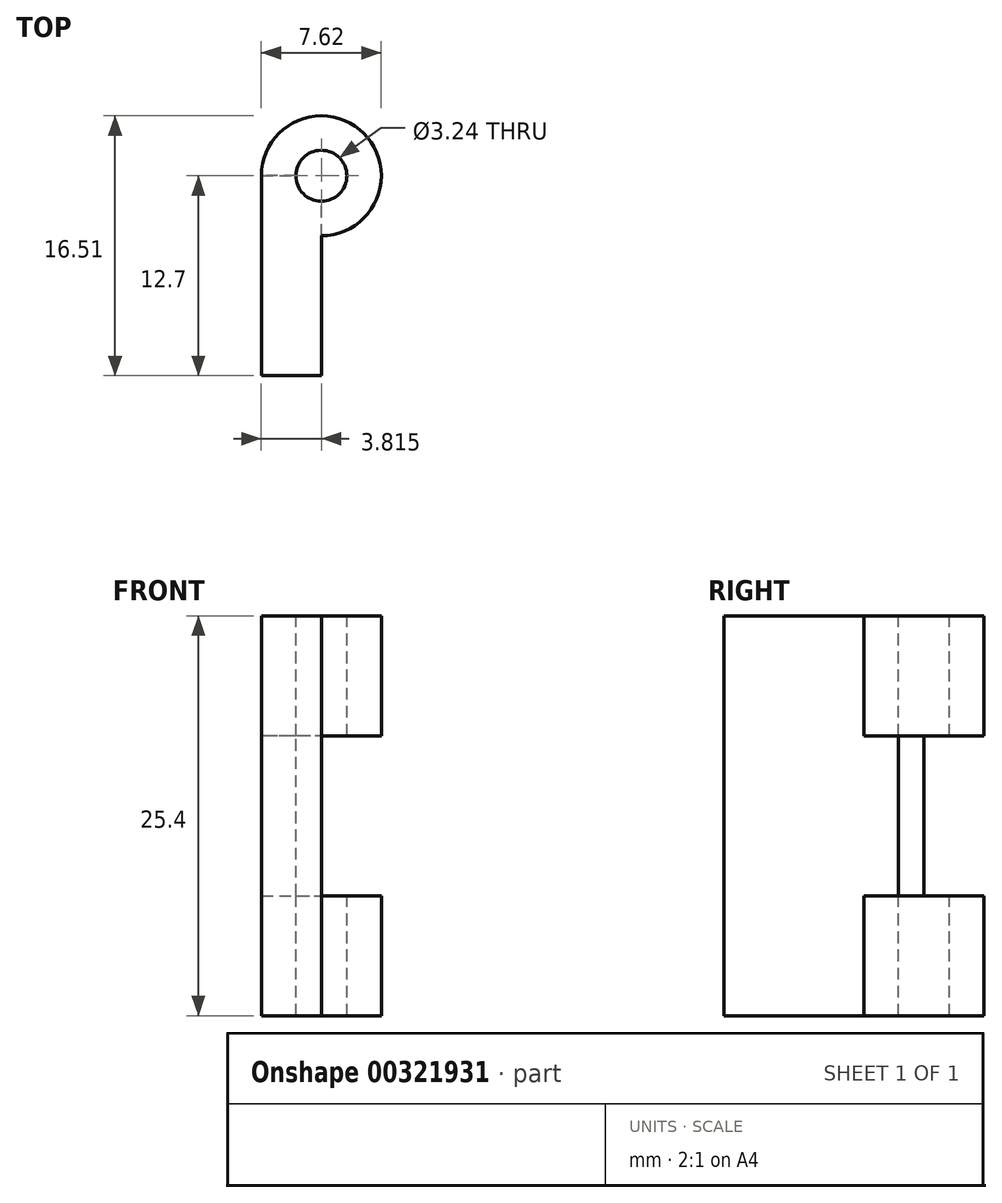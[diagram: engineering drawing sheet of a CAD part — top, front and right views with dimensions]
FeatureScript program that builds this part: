
annotation { "Feature Type Name" : "Feature", "Feature Type Description" : "" }
export const myFeature = defineFeature(function(context is Context, id is Id, definition is map)
    precondition{}
    {
        {
            var Q0;
            Q0=qCreatedBy(makeId("Front.planeOp"),FACE);
            var sketch = newSketch(context, id + "F0", { "sketchPlane" : qUnion([Q0])});
            skLineSegment(sketch, "E0.bottom", {"start": v(-1.9, -12.7) * mm, "end": v(1.9, -12.7) * mm});
            skLineSegment(sketch, "E0.top", {"start": v(-1.9, 12.7) * mm, "end": v(1.9, 12.7) * mm});
            skLineSegment(sketch, "E0.left", {"start": v(-1.9, -12.7) * mm, "end": v(-1.9, 12.7) * mm});
            skLineSegment(sketch, "E0.right", {"start": v(1.9, -12.7) * mm, "end": v(1.9, 12.7) * mm});
            skPoint(sketch, "E0.middle", {"position": v(0, 0) * mm});
            skSolve(sketch);
        }
        {
            var Q0;
            Q0 = qSketchRegion(id + "F0", true);
            extrude(context, id + "F1", {"entities" : qUnion([Q0]), "depth" : 12.7 * mm});
        }
        {
            var Q0;
            Q0=makeQuery(id+"F1.opExtrude","SWEPT_FACE",FACE,{"disambiguationData":[OSD([sQuery(id+"F0.wireOp",EDGE,"E0.top")])]});
            var sketch = newSketch(context, id + "F2", { "sketchPlane" : qUnion([Q0])});
            skCircle(sketch, "E1", {"center": v(1.9, 0) * mm, "radius": 3.81 * mm});
            skSolve(sketch);
        }
        {
            var Q0;
            Q0 = qSketchRegion(id + "F2", true);
            extrude(context, id + "F3", {"entities" : qUnion([Q0]), "operationType" : NewBodyOperationType.ADD, "oppositeDirection" : true, "depth" : 7.62 * mm});
        }
        {
            var Q0;
            Q0=makeQuery(id+"F1.opExtrude","SWEPT_FACE",FACE,{"disambiguationData":[OSD([sQuery(id+"F0.wireOp",EDGE,"E0.bottom")])]});
            var sketch = newSketch(context, id + "F4", { "sketchPlane" : qUnion([Q0])});
            skCircle(sketch, "E2", {"center": v(1.9, 0) * mm, "radius": 3.81 * mm});
            skSolve(sketch);
        }
        {
            var Q0;
            Q0 = qSketchRegion(id + "F2", true);
            extrude(context, id + "F5", {"entities" : qUnion([Q0]), "operationType" : NewBodyOperationType.ADD, "oppositeDirection" : true, "depth" : 7.62 * mm});
        }
        {
            var Q0;
            {var subQ1=sQuery(id+"F0.wireOp",EDGE,"E0.bottom");var subQ2=makeQuery(id+"F1.opExtrude","CAP_EDGE",EDGE,{"disambiguationData":[OSD([subQ1])],"isStart":true});Q0=makeQuery(id+"F4.imprint","IMPRINT",FACE,{"disambiguationData":[TD([[makeQuery(id+"F4.imprint","IMPRINT",EDGE,{"derivedFrom":subQ2}),-1.0]])]});}
            extrude(context, id + "F6", {"entities" : qUnion([Q0]), "operationType" : NewBodyOperationType.ADD, "oppositeDirection" : true, "depth" : 7.62 * mm});
        }
        {
            var Q0;
            Q0=makeQuery(id+"F3.boolean.opBoolean","MERGE",FACE,{"derivedFrom":[makeQuery(id+"F1.opExtrude","SWEPT_FACE",FACE,{"disambiguationData":[OSD([sQuery(id+"F0.wireOp",EDGE,"E0.top")])]}),makeQuery(id+"F3.opExtrude","CAP_FACE",FACE,{"disambiguationData":[OSD([sQuery(id+"F2.wireOp",EDGE,"E1")])],"isStart":true})]});
            var sketch = newSketch(context, id + "F7", { "sketchPlane" : qUnion([Q0])});
            skLineSegment(sketch, "E3", {"start": v(1.9, -3.81) * mm, "end": v(1.9, 3.81) * mm, "construction": true});
            skCircle(sketch, "E4", {"center": v(1.9, 0) * mm, "radius": 1.62 * mm});
            skSolve(sketch);
        }
        {
            var Q0;
            Q0 = qSketchRegion(id + "F7", true);
            extrude(context, id + "F8", {"entities" : qUnion([Q0]), "operationType" : NewBodyOperationType.REMOVE, "oppositeDirection" : true, "depth" : 25.4 * mm});
        }
    });
